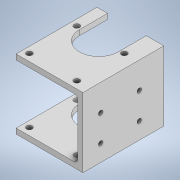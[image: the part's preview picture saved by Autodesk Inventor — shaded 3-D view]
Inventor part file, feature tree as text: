
AUTODESK INVENTOR PART (.ipt)
format: ipt  version: 2022 (Build 260153000, 153)  size: 186,368 bytes
history: native  units: mm
features: sketch x6, extrude x3, hole x3, other x1, fillet x1
ambient origin geometry x8: Origin, YZ Plane, XZ Plane, XY Plane, X Axis, Y Axis, Z Axis, Center Point
bodies: Body1 (feature_tree)
feature tree (14):
  other  "ソリッド1"
  extrude  "押し出し1"  Depth=46.0mm
  extrude  "押し出し2"  Depth=38.0mm
  hole  "穴1"  [1 undecoded]
  hole  "穴2"  [1 undecoded]
  fillet  "フィレット1"  Radius=3.0mm
  extrude  "押し出し3"  Depth=3.0mm
  hole  "穴5"  [1 undecoded]
  sketch  "スケッチ1"
  sketch  "スケッチ2"
  sketch  "スケッチ3"
  sketch  "スケッチ4"
  sketch  "スケッチ7"
  sketch  "スケッチ8"
note: 3 required parameter values undecoded (feature->parameter linkage not recoverable at this tier; creation-order binding heuristic only, values carry confidence <= 0.55)
